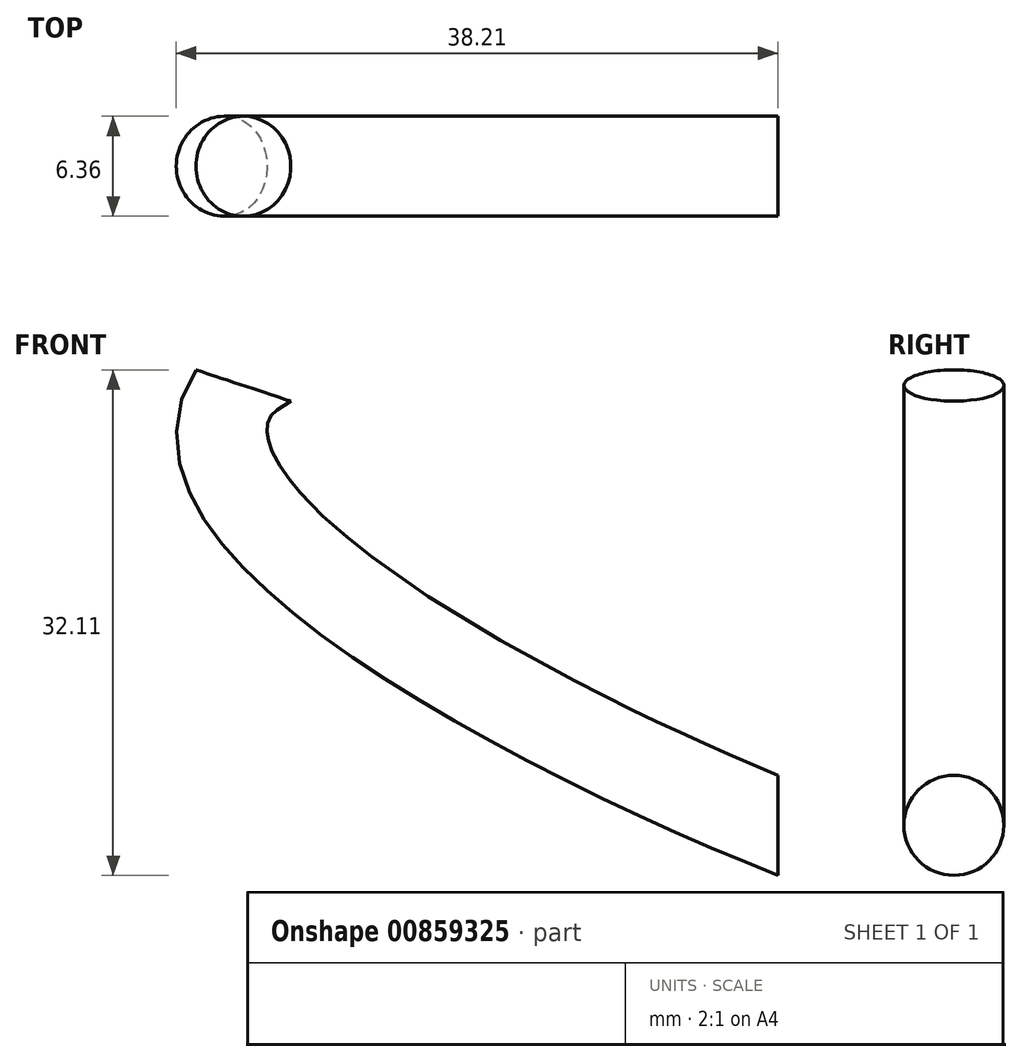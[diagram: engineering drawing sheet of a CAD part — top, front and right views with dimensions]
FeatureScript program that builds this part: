
annotation { "Feature Type Name" : "Feature", "Feature Type Description" : "" }
export const myFeature = defineFeature(function(context is Context, id is Id, definition is map)
    precondition{}
    {
        {
            var Q0;
            Q0=qCreatedBy(makeId("Front.planeOp"),FACE);
            var sketch = newSketch(context, id + "F0", { "sketchPlane" : qUnion([Q0])});
            skFitSpline(sketch, "E0", {"points": [v(0, 0) * mm, v(-33.95, 27.93) * mm], "startDerivative": vector(-45.23, 18.31) * mm, "endDerivative": vector(21.52, 25.36) * mm});
            skSolve(sketch);
        }
        {
            var Q0;
            Q0=qCreatedBy(makeId("Right.planeOp"),FACE);
            var sketch = newSketch(context, id + "F1", { "sketchPlane" : qUnion([Q0])});
            skCircle(sketch, "E1", {"center": v(0, 0) * mm, "radius": 3.18 * mm});
            skSolve(sketch);
        }
        {
            var Q0;
            Q0=makeQuery(id+"F1.imprint","IMPRINT",FACE,{"disambiguationData":[TD([[makeQuery(id+"F1.imprint","IMPRINT",EDGE,{"derivedFrom":sQuery(id+"F1.wireOp",EDGE,"E1")}),1.0]])]});
            var Q1;
            Q1=sQuery(id+"F0.wireOp",EDGE,"E0");
            sweep(context, id + "F2", {"profiles" : qUnion([Q0]), "path" : qUnion([Q1])});
        }
    });
